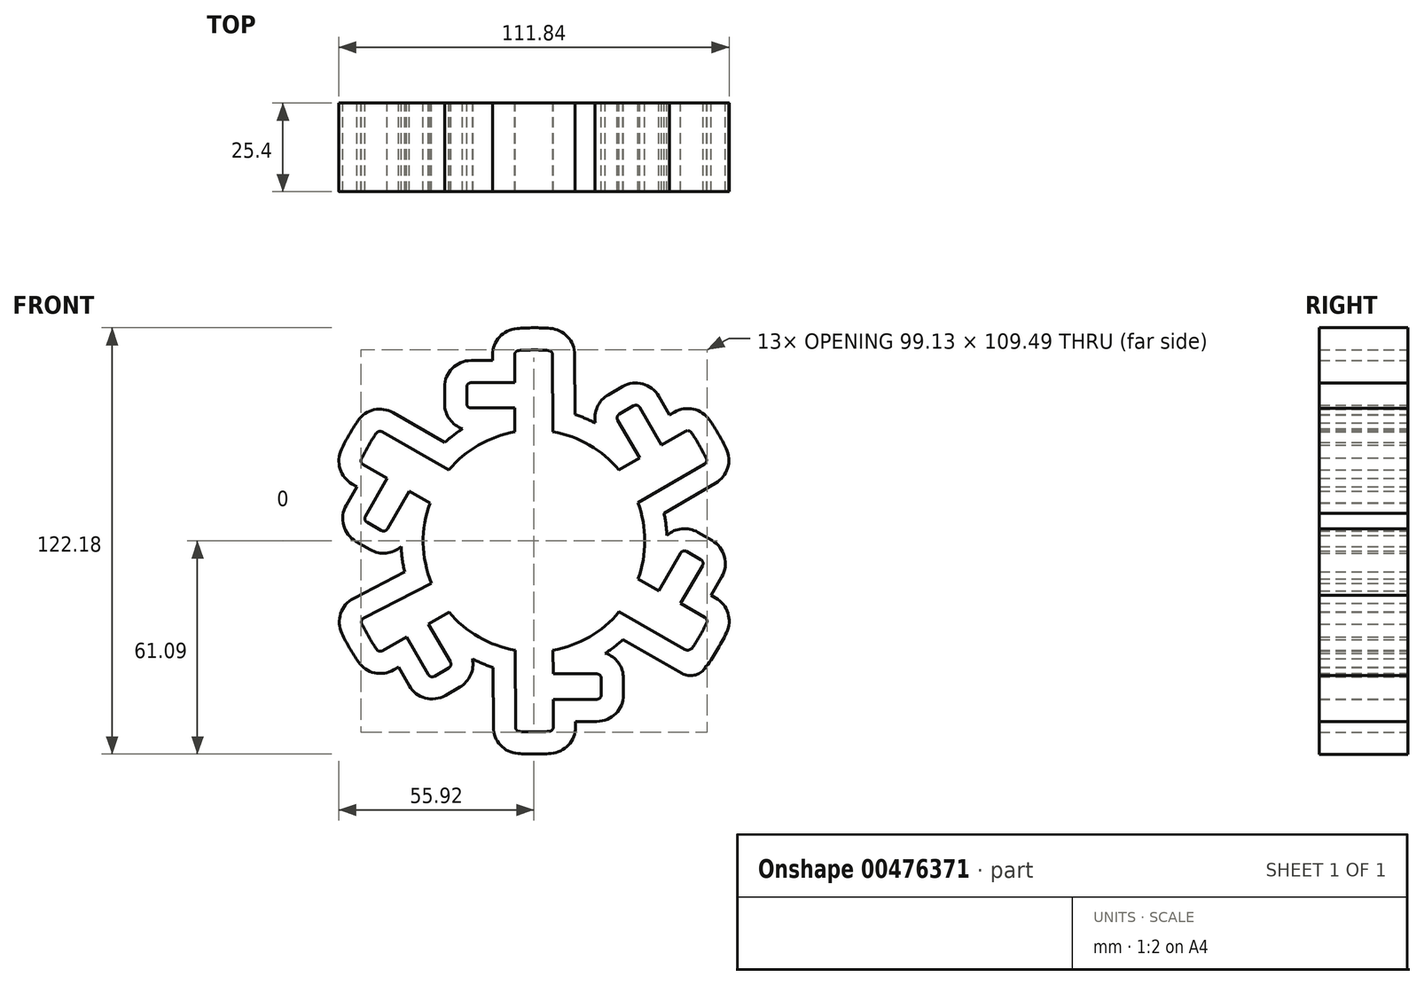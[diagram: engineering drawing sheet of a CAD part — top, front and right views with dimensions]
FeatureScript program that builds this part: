
annotation { "Feature Type Name" : "Feature", "Feature Type Description" : "" }
export const myFeature = defineFeature(function(context is Context, id is Id, definition is map)
    precondition{}
    {
        {
            var Q0;
            Q0=qCreatedBy(makeId("Front.planeOp"),FACE);
            var sketch = newSketch(context, id + "F0", { "sketchPlane" : qUnion([Q0])});
            skArc(sketch, "E0", {"start": v(5.31, 54.48) * mm, "mid": v(-0.12, 54.74) * mm, "end": v(-5.54, 54.46) * mm});
            skArc(sketch, "E1", {"start": v(-5.45, 31.28) * mm, "mid": v(-15.9, 27.48) * mm, "end": v(-24.4, 20.32) * mm});
            skLineSegment(sketch, "E2.left", {"start": v(-5.45, 31.28) * mm, "end": v(-5.48, 38.1) * mm});
            skLineSegment(sketch, "E2.right", {"start": v(5.4, 31.29) * mm, "end": v(5.31, 54.48) * mm});
            skLineSegment(sketch, "E3.bottom", {"start": v(-5.48, 38.1) * mm, "end": v(-19.28, 38.1) * mm});
            skLineSegment(sketch, "E3.top", {"start": v(-5.5, 45.36) * mm, "end": v(-19.28, 45.36) * mm});
            skLineSegment(sketch, "E3.left", {"start": v(5.38, 38.1) * mm, "end": v(5.38, 45.36) * mm});
            skLineSegment(sketch, "E3.right", {"start": v(-19.28, 38.1) * mm, "end": v(-19.28, 45.36) * mm});
            skLineSegment(sketch, "E4.trimOffspring", {"start": v(-5.5, 45.36) * mm, "end": v(-5.54, 54.46) * mm});
            skLineSegment(sketch, "E5.1.0", {"start": v(-30.3, 23.7) * mm, "end": v(-36.6, 27.34) * mm});
            skLineSegment(sketch, "E5.1.1", {"start": v(-24.4, 20.32) * mm, "end": v(-44.53, 31.84) * mm});
            skArc(sketch, "E5.1.2", {"start": v(-44.53, 31.84) * mm, "mid": v(-47.47, 27.27) * mm, "end": v(-49.94, 22.43) * mm});
            skLineSegment(sketch, "E5.1.3", {"start": v(-42.04, 17.9) * mm, "end": v(-49.94, 22.43) * mm});
            skLineSegment(sketch, "E5.1.4", {"start": v(-29.81, 10.92) * mm, "end": v(-35.74, 14.3) * mm});
            skLineSegment(sketch, "E5.1.5", {"start": v(-35.74, 14.3) * mm, "end": v(-42.64, 2.35) * mm});
            skLineSegment(sketch, "E5.1.6", {"start": v(-42.64, 2.35) * mm, "end": v(-48.92, 5.98) * mm});
            skLineSegment(sketch, "E5.1.7", {"start": v(-42.04, 17.9) * mm, "end": v(-48.92, 5.98) * mm});
            skArc(sketch, "E5.2.2", {"start": v(-49.84, -22.64) * mm, "mid": v(-47.35, -27.47) * mm, "end": v(-44.4, -32.03) * mm});
            skLineSegment(sketch, "E5.2.3", {"start": v(-36.53, -27.45) * mm, "end": v(-44.4, -32.03) * mm});
            skLineSegment(sketch, "E5.2.4", {"start": v(-24.36, -20.36) * mm, "end": v(-30.26, -23.8) * mm});
            skLineSegment(sketch, "E5.2.5", {"start": v(-30.26, -23.8) * mm, "end": v(-23.35, -35.75) * mm});
            skLineSegment(sketch, "E5.2.6", {"start": v(-23.35, -35.75) * mm, "end": v(-29.64, -39.38) * mm});
            skLineSegment(sketch, "E5.2.7", {"start": v(-36.53, -27.45) * mm, "end": v(-29.64, -39.38) * mm});
            skLineSegment(sketch, "E5.3.1", {"start": v(-5.4, -31.29) * mm, "end": v(-5.31, -54.48) * mm});
            skArc(sketch, "E5.3.2", {"start": v(-5.31, -54.48) * mm, "mid": v(0.12, -54.74) * mm, "end": v(5.54, -54.46) * mm});
            skLineSegment(sketch, "E5.3.3", {"start": v(5.5, -45.36) * mm, "end": v(5.54, -54.46) * mm});
            skLineSegment(sketch, "E5.3.4", {"start": v(5.45, -31.28) * mm, "end": v(5.48, -38.1) * mm});
            skLineSegment(sketch, "E5.3.5", {"start": v(5.48, -38.1) * mm, "end": v(19.28, -38.1) * mm});
            skLineSegment(sketch, "E5.3.6", {"start": v(19.28, -38.1) * mm, "end": v(19.28, -45.36) * mm});
            skLineSegment(sketch, "E5.3.7", {"start": v(5.5, -45.36) * mm, "end": v(19.28, -45.36) * mm});
            skLineSegment(sketch, "E5.4.0", {"start": v(30.3, -23.7) * mm, "end": v(36.6, -27.34) * mm});
            skLineSegment(sketch, "E5.4.1", {"start": v(24.4, -20.32) * mm, "end": v(44.53, -31.84) * mm});
            skArc(sketch, "E5.4.2", {"start": v(44.53, -31.84) * mm, "mid": v(47.47, -27.27) * mm, "end": v(49.94, -22.43) * mm});
            skLineSegment(sketch, "E5.4.3", {"start": v(42.04, -17.9) * mm, "end": v(49.94, -22.43) * mm});
            skLineSegment(sketch, "E5.4.4", {"start": v(29.81, -10.92) * mm, "end": v(35.74, -14.3) * mm});
            skLineSegment(sketch, "E5.4.5", {"start": v(35.74, -14.3) * mm, "end": v(42.64, -2.35) * mm});
            skLineSegment(sketch, "E5.4.6", {"start": v(42.64, -2.35) * mm, "end": v(48.92, -5.98) * mm});
            skLineSegment(sketch, "E5.4.7", {"start": v(42.04, -17.9) * mm, "end": v(48.92, -5.98) * mm});
            skLineSegment(sketch, "E6.3.5.0", {"start": v(29.8, 10.96) * mm, "end": v(49.84, 22.64) * mm});
            skArc(sketch, "E6.6.5.0", {"start": v(49.84, 22.64) * mm, "mid": v(47.35, 27.47) * mm, "end": v(44.4, 32.03) * mm});
            skLineSegment(sketch, "E6.10.5.0", {"start": v(36.53, 27.45) * mm, "end": v(44.4, 32.03) * mm});
            skLineSegment(sketch, "E6.13.5.0", {"start": v(24.36, 20.36) * mm, "end": v(30.26, 23.8) * mm});
            skLineSegment(sketch, "E6.16.5.0", {"start": v(30.26, 23.8) * mm, "end": v(23.35, 35.75) * mm});
            skLineSegment(sketch, "E6.19.5.0", {"start": v(23.35, 35.75) * mm, "end": v(29.64, 39.38) * mm});
            skLineSegment(sketch, "E6.22.5.0", {"start": v(36.53, 27.45) * mm, "end": v(29.64, 39.38) * mm});
            skLineSegment(sketch, "E7", {"start": v(-49.84, -22.64) * mm, "end": v(-29.37, -12.07) * mm});
            skArc(sketch, "E8.trimOffspring", {"start": v(24.36, 20.36) * mm, "mid": v(15.85, 27.5) * mm, "end": v(5.4, 31.29) * mm});
            skArc(sketch, "E9.trimOffspring", {"start": v(29.81, -10.92) * mm, "mid": v(31.75, 0.03) * mm, "end": v(29.8, 10.96) * mm});
            skArc(sketch, "E10.trimOffspring", {"start": v(5.45, -31.28) * mm, "mid": v(15.9, -27.48) * mm, "end": v(24.4, -20.32) * mm});
            skArc(sketch, "E11.trimOffspring", {"start": v(-24.36, -20.36) * mm, "mid": v(-15.85, -27.5) * mm, "end": v(-5.4, -31.29) * mm});
            skArc(sketch, "E12.trimOffspring", {"start": v(-29.81, 10.92) * mm, "mid": v(-31.74, -0.62) * mm, "end": v(-29.37, -12.07) * mm});
            skSolve(sketch);
        }
        {
            var Q0;
            {var subQ0=sQuery(id+"F0.wireOp",EDGE,"E1");var subQ5=makeQuery(id+"F0.imprint","INTERSECT",VERTEX,{"derivedFrom":[subQ0,sQuery(id+"F0.wireOp",EDGE,"E5.4.1")]});Q0=makeQuery(id+"F0.imprint","IMPRINT",FACE,{"disambiguationData":[TD([[makeQuery(id+"F0.imprint","IMPRINT",EDGE,{"disambiguationData":[TD([[subQ5,-1.0]])],"derivedFrom":subQ0}),1.0]])]});}
            var Q1;
            {var subQ0=sQuery(id+"F0.wireOp",EDGE,"E5.1.2");Q1=makeQuery(id+"F0.imprint","IMPRINT",FACE,{"disambiguationData":[TD([[makeQuery(id+"F0.imprint","IMPRINT",EDGE,{"derivedFrom":subQ0}),1.0]])]});}
            var Q2;
            {var subQ5=sQuery(id+"F0.wireOp",EDGE,"E0");Q2=makeQuery(id+"F0.imprint","IMPRINT",FACE,{"disambiguationData":[TD([[makeQuery(id+"F0.imprint","IMPRINT",EDGE,{"derivedFrom":subQ5}),1.0]])]});}
            var Q3;
            {var subQ0=sQuery(id+"F0.wireOp",EDGE,"E5.4.2");Q3=makeQuery(id+"F0.imprint","IMPRINT",FACE,{"disambiguationData":[TD([[makeQuery(id+"F0.imprint","IMPRINT",EDGE,{"derivedFrom":subQ0}),1.0]])]});}
            var Q4;
            {var subQ0=sQuery(id+"F0.wireOp",EDGE,"E5.3.2");Q4=makeQuery(id+"F0.imprint","IMPRINT",FACE,{"disambiguationData":[TD([[makeQuery(id+"F0.imprint","IMPRINT",EDGE,{"derivedFrom":subQ0}),1.0]])]});}
            var Q5;
            {var subQ0=sQuery(id+"F0.wireOp",EDGE,"E5.2.2");Q5=makeQuery(id+"F0.imprint","IMPRINT",FACE,{"disambiguationData":[TD([[makeQuery(id+"F0.imprint","IMPRINT",EDGE,{"derivedFrom":subQ0}),1.0]])]});}
            var Q6;
            {var subQ0=sQuery(id+"F0.wireOp",EDGE,"E6.6.5.0");Q6=makeQuery(id+"F0.imprint","IMPRINT",FACE,{"disambiguationData":[TD([[makeQuery(id+"F0.imprint","IMPRINT",EDGE,{"derivedFrom":subQ0}),1.0]])]});}
            extrude(context, id + "F1", {"entities" : qUnion([Q0, Q1, Q2, Q3, Q4, Q5, Q6]), "depth" : 25.4 * mm});
        }
        {
            var Q0;
            Q0=makeQuery(id+"F1.opExtrude","SWEPT_EDGE",EDGE,{"disambiguationData":[OSD([sQuery(id+"F0.wireOp",EDGE,"E0"),sQuery(id+"F0.wireOp",EDGE,"E2.right")])]});
            var Q1;
            Q1=makeQuery(id+"F1.opExtrude","SWEPT_EDGE",EDGE,{"disambiguationData":[OSD([sQuery(id+"F0.wireOp",EDGE,"E0"),sQuery(id+"F0.wireOp",EDGE,"E4.trimOffspring")])]});
            fillet(context, id + "F2", {"entities" : qUnion([Q0, Q1]), "radius" : 1.27 * mm, "tangentPropagation" : true, "allowEdgeOverflow" : false});
        }
        {
            var Q0;
            Q0=makeQuery(id+"F1.opExtrude","SWEPT_EDGE",EDGE,{"disambiguationData":[OSD([sQuery(id+"F0.wireOp",EDGE,"E3.top"),sQuery(id+"F0.wireOp",EDGE,"E3.right")])]});
            var Q1;
            Q1=makeQuery(id+"F1.opExtrude","SWEPT_EDGE",EDGE,{"disambiguationData":[OSD([sQuery(id+"F0.wireOp",EDGE,"E3.bottom"),sQuery(id+"F0.wireOp",EDGE,"E3.right")])]});
            fillet(context, id + "F3", {"entities" : qUnion([Q0, Q1]), "radius" : 1.27 * mm, "tangentPropagation" : true, "allowEdgeOverflow" : false});
        }
        {
            var Q0;
            Q0=makeQuery(id+"F1.opExtrude","SWEPT_EDGE",EDGE,{"disambiguationData":[OSD([sQuery(id+"F0.wireOp",EDGE,"E6.19.5.0"),sQuery(id+"F0.wireOp",EDGE,"E6.22.5.0")])]});
            var Q1;
            Q1=makeQuery(id+"F1.opExtrude","SWEPT_EDGE",EDGE,{"disambiguationData":[OSD([sQuery(id+"F0.wireOp",EDGE,"E6.16.5.0"),sQuery(id+"F0.wireOp",EDGE,"E6.19.5.0")])]});
            var Q2;
            Q2=makeQuery(id+"F1.opExtrude","SWEPT_EDGE",EDGE,{"disambiguationData":[OSD([sQuery(id+"F0.wireOp",EDGE,"E6.6.5.0"),sQuery(id+"F0.wireOp",EDGE,"E6.10.5.0")])]});
            var Q3;
            Q3=makeQuery(id+"F1.opExtrude","SWEPT_EDGE",EDGE,{"disambiguationData":[OSD([sQuery(id+"F0.wireOp",EDGE,"E6.3.5.0"),sQuery(id+"F0.wireOp",EDGE,"E6.6.5.0")])]});
            var Q4;
            Q4=makeQuery(id+"F1.opExtrude","SWEPT_EDGE",EDGE,{"disambiguationData":[OSD([sQuery(id+"F0.wireOp",EDGE,"E5.4.6"),sQuery(id+"F0.wireOp",EDGE,"E5.4.7")])]});
            var Q5;
            Q5=makeQuery(id+"F1.opExtrude","SWEPT_EDGE",EDGE,{"disambiguationData":[OSD([sQuery(id+"F0.wireOp",EDGE,"E5.4.2"),sQuery(id+"F0.wireOp",EDGE,"E5.4.3")])]});
            var Q6;
            Q6=makeQuery(id+"F1.opExtrude","SWEPT_EDGE",EDGE,{"disambiguationData":[OSD([sQuery(id+"F0.wireOp",EDGE,"E5.4.5"),sQuery(id+"F0.wireOp",EDGE,"E5.4.6")])]});
            var Q7;
            Q7=makeQuery(id+"F1.opExtrude","SWEPT_EDGE",EDGE,{"disambiguationData":[OSD([sQuery(id+"F0.wireOp",EDGE,"E5.3.6"),sQuery(id+"F0.wireOp",EDGE,"E5.3.7")])]});
            var Q8;
            Q8=makeQuery(id+"F1.opExtrude","SWEPT_EDGE",EDGE,{"disambiguationData":[OSD([sQuery(id+"F0.wireOp",EDGE,"E5.3.5"),sQuery(id+"F0.wireOp",EDGE,"E5.3.6")])]});
            var Q9;
            Q9=makeQuery(id+"F1.opExtrude","SWEPT_EDGE",EDGE,{"disambiguationData":[OSD([sQuery(id+"F0.wireOp",EDGE,"E5.3.2"),sQuery(id+"F0.wireOp",EDGE,"E5.3.3")])]});
            var Q10;
            Q10=makeQuery(id+"F1.opExtrude","SWEPT_EDGE",EDGE,{"disambiguationData":[OSD([sQuery(id+"F0.wireOp",EDGE,"E5.3.1"),sQuery(id+"F0.wireOp",EDGE,"E5.3.2")])]});
            var Q11;
            Q11=makeQuery(id+"F1.opExtrude","SWEPT_EDGE",EDGE,{"disambiguationData":[OSD([sQuery(id+"F0.wireOp",EDGE,"E5.2.6"),sQuery(id+"F0.wireOp",EDGE,"E5.2.7")])]});
            var Q12;
            Q12=makeQuery(id+"F1.opExtrude","SWEPT_EDGE",EDGE,{"disambiguationData":[OSD([sQuery(id+"F0.wireOp",EDGE,"E5.2.5"),sQuery(id+"F0.wireOp",EDGE,"E5.2.6")])]});
            var Q13;
            Q13=makeQuery(id+"F1.opExtrude","SWEPT_EDGE",EDGE,{"disambiguationData":[OSD([sQuery(id+"F0.wireOp",EDGE,"E5.2.2"),sQuery(id+"F0.wireOp",EDGE,"E5.2.3")])]});
            var Q14;
            Q14=makeQuery(id+"F1.opExtrude","SWEPT_EDGE",EDGE,{"disambiguationData":[OSD([sQuery(id+"F0.wireOp",EDGE,"E5.2.1"),sQuery(id+"F0.wireOp",EDGE,"E5.2.2")])]});
            var Q15;
            Q15=makeQuery(id+"F1.opExtrude","SWEPT_EDGE",EDGE,{"disambiguationData":[OSD([sQuery(id+"F0.wireOp",EDGE,"E5.1.6"),sQuery(id+"F0.wireOp",EDGE,"E5.1.7")])]});
            var Q16;
            Q16=makeQuery(id+"F1.opExtrude","SWEPT_EDGE",EDGE,{"disambiguationData":[OSD([sQuery(id+"F0.wireOp",EDGE,"E5.1.5"),sQuery(id+"F0.wireOp",EDGE,"E5.1.6")])]});
            var Q17;
            Q17=makeQuery(id+"F1.opExtrude","SWEPT_EDGE",EDGE,{"disambiguationData":[OSD([sQuery(id+"F0.wireOp",EDGE,"E5.1.2"),sQuery(id+"F0.wireOp",EDGE,"E5.1.3")])]});
            var Q18;
            Q18=makeQuery(id+"F1.opExtrude","SWEPT_EDGE",EDGE,{"disambiguationData":[OSD([sQuery(id+"F0.wireOp",EDGE,"E5.1.1"),sQuery(id+"F0.wireOp",EDGE,"E5.1.2")])]});
            fillet(context, id + "F4", {"entities" : qUnion([Q0, Q1, Q2, Q3, Q4, Q5, Q6, Q7, Q8, Q9, Q10, Q11, Q12, Q13, Q14, Q15, Q16, Q17, Q18]), "radius" : 1.27 * mm, "tangentPropagation" : true, "allowEdgeOverflow" : false});
        }
        {
            var Q0;
            Q0=makeQuery(id+"F1.opExtrude","CAP_FACE",FACE,{"disambiguationData":[OSD([sQuery(id+"F0.wireOp",EDGE,"E0"),sQuery(id+"F0.wireOp",EDGE,"E1"),sQuery(id+"F0.wireOp",EDGE,"E2.left"),sQuery(id+"F0.wireOp",EDGE,"E2.right"),sQuery(id+"F0.wireOp",EDGE,"E3.bottom"),sQuery(id+"F0.wireOp",EDGE,"E3.top"),sQuery(id+"F0.wireOp",EDGE,"E3.right"),sQuery(id+"F0.wireOp",EDGE,"E4.trimOffspring"),sQuery(id+"F0.wireOp",EDGE,"E5.1.1"),sQuery(id+"F0.wireOp",EDGE,"E5.1.2"),sQuery(id+"F0.wireOp",EDGE,"E5.1.3"),sQuery(id+"F0.wireOp",EDGE,"E5.1.4"),sQuery(id+"F0.wireOp",EDGE,"E5.1.5"),sQuery(id+"F0.wireOp",EDGE,"E5.1.6"),sQuery(id+"F0.wireOp",EDGE,"E5.1.7"),sQuery(id+"F0.wireOp",EDGE,"E5.2.2"),sQuery(id+"F0.wireOp",EDGE,"E5.2.3"),sQuery(id+"F0.wireOp",EDGE,"E5.2.4"),sQuery(id+"F0.wireOp",EDGE,"E5.2.5"),sQuery(id+"F0.wireOp",EDGE,"E5.2.6"),sQuery(id+"F0.wireOp",EDGE,"E5.2.7"),sQuery(id+"F0.wireOp",EDGE,"E5.3.1"),sQuery(id+"F0.wireOp",EDGE,"E5.3.2"),sQuery(id+"F0.wireOp",EDGE,"E5.3.3"),sQuery(id+"F0.wireOp",EDGE,"E5.3.4"),sQuery(id+"F0.wireOp",EDGE,"E5.3.5"),sQuery(id+"F0.wireOp",EDGE,"E5.3.6"),sQuery(id+"F0.wireOp",EDGE,"E5.3.7"),sQuery(id+"F0.wireOp",EDGE,"E5.4.1"),sQuery(id+"F0.wireOp",EDGE,"E5.4.2"),sQuery(id+"F0.wireOp",EDGE,"E5.4.3"),sQuery(id+"F0.wireOp",EDGE,"E5.4.4"),sQuery(id+"F0.wireOp",EDGE,"E5.4.5"),sQuery(id+"F0.wireOp",EDGE,"E5.4.6"),sQuery(id+"F0.wireOp",EDGE,"E5.4.7"),sQuery(id+"F0.wireOp",EDGE,"E6.3.5.0"),sQuery(id+"F0.wireOp",EDGE,"E6.6.5.0"),sQuery(id+"F0.wireOp",EDGE,"E6.10.5.0"),sQuery(id+"F0.wireOp",EDGE,"E6.13.5.0"),sQuery(id+"F0.wireOp",EDGE,"E6.16.5.0"),sQuery(id+"F0.wireOp",EDGE,"E6.19.5.0"),sQuery(id+"F0.wireOp",EDGE,"E6.22.5.0"),sQuery(id+"F0.wireOp",EDGE,"E7"),sQuery(id+"F0.wireOp",EDGE,"E8.trimOffspring"),sQuery(id+"F0.wireOp",EDGE,"E9.trimOffspring"),sQuery(id+"F0.wireOp",EDGE,"E10.trimOffspring"),sQuery(id+"F0.wireOp",EDGE,"E11.trimOffspring"),sQuery(id+"F0.wireOp",EDGE,"E12.trimOffspring")])],"isStart":false});
            var sketch = newSketch(context, id + "F5", { "sketchPlane" : qUnion([Q0])});
            skLineSegment(sketch, "E13.0.0", {"start": v(-24.4, 20.32) * mm, "end": v(-43.52, 31.27) * mm});
            skArc(sketch, "E13.0.1", {"start": v(-43.52, 31.27) * mm, "mid": v(-44.44, 31.4) * mm, "end": v(-45.2, 30.88) * mm});
            skArc(sketch, "E13.0.2", {"start": v(-45.2, 30.88) * mm, "mid": v(-47.47, 27.27) * mm, "end": v(-49.44, 23.5) * mm});
            skArc(sketch, "E13.0.3", {"start": v(-49.44, 23.5) * mm, "mid": v(-49.5, 22.57) * mm, "end": v(-48.93, 21.85) * mm});
            skLineSegment(sketch, "E13.0.4", {"start": v(-48.93, 21.85) * mm, "end": v(-42.04, 17.9) * mm});
            skLineSegment(sketch, "E13.0.5", {"start": v(-42.04, 17.9) * mm, "end": v(-48.29, 7.08) * mm});
            skArc(sketch, "E13.0.6", {"start": v(-48.29, 7.08) * mm, "mid": v(-48.42, 6.12) * mm, "end": v(-47.82, 5.34) * mm});
            skLineSegment(sketch, "E13.0.7", {"start": v(-47.82, 5.34) * mm, "end": v(-43.74, 2.98) * mm});
            skArc(sketch, "E13.0.8", {"start": v(-43.74, 2.98) * mm, "mid": v(-42.77, 2.86) * mm, "end": v(-42, 3.45) * mm});
            skLineSegment(sketch, "E13.0.9", {"start": v(-42, 3.45) * mm, "end": v(-35.74, 14.3) * mm});
            skLineSegment(sketch, "E13.0.10", {"start": v(-35.74, 14.3) * mm, "end": v(-29.81, 10.92) * mm});
            skArc(sketch, "E13.0.11", {"start": v(-29.81, 10.92) * mm, "mid": v(-31.74, -0.62) * mm, "end": v(-29.37, -12.07) * mm});
            skLineSegment(sketch, "E13.0.12", {"start": v(-29.37, -12.07) * mm, "end": v(-48.76, -22.08) * mm});
            skArc(sketch, "E13.0.13", {"start": v(-48.76, -22.08) * mm, "mid": v(-49.38, -22.8) * mm, "end": v(-49.32, -23.76) * mm});
            skArc(sketch, "E13.0.14", {"start": v(-49.32, -23.76) * mm, "mid": v(-47.34, -27.5) * mm, "end": v(-45.07, -31.07) * mm});
            skArc(sketch, "E13.0.15", {"start": v(-45.07, -31.07) * mm, "mid": v(-44.3, -31.59) * mm, "end": v(-43.39, -31.45) * mm});
            skLineSegment(sketch, "E13.0.16", {"start": v(-43.39, -31.45) * mm, "end": v(-36.53, -27.45) * mm});
            skLineSegment(sketch, "E13.0.17", {"start": v(-36.53, -27.45) * mm, "end": v(-30.28, -38.28) * mm});
            skArc(sketch, "E13.0.18", {"start": v(-30.28, -38.28) * mm, "mid": v(-29.5, -38.87) * mm, "end": v(-28.54, -38.75) * mm});
            skLineSegment(sketch, "E13.0.19", {"start": v(-28.54, -38.75) * mm, "end": v(-24.45, -36.39) * mm});
            skArc(sketch, "E13.0.20", {"start": v(-24.45, -36.39) * mm, "mid": v(-23.86, -35.61) * mm, "end": v(-23.99, -34.65) * mm});
            skLineSegment(sketch, "E13.0.21", {"start": v(-23.99, -34.65) * mm, "end": v(-30.26, -23.8) * mm});
            skLineSegment(sketch, "E13.0.22", {"start": v(-30.26, -23.8) * mm, "end": v(-24.36, -20.36) * mm});
            skArc(sketch, "E13.0.23", {"start": v(-24.36, -20.36) * mm, "mid": v(-15.85, -27.5) * mm, "end": v(-5.4, -31.29) * mm});
            skLineSegment(sketch, "E13.0.24", {"start": v(-5.4, -31.29) * mm, "end": v(-5.32, -53.32) * mm});
            skArc(sketch, "E13.0.25", {"start": v(-5.32, -53.32) * mm, "mid": v(-4.98, -54.19) * mm, "end": v(-4.14, -54.59) * mm});
            skArc(sketch, "E13.0.26", {"start": v(-4.14, -54.59) * mm, "mid": v(0.12, -54.74) * mm, "end": v(4.37, -54.57) * mm});
            skArc(sketch, "E13.0.27", {"start": v(4.37, -54.57) * mm, "mid": v(5.2, -54.16) * mm, "end": v(5.54, -53.3) * mm});
            skLineSegment(sketch, "E13.0.28", {"start": v(5.54, -53.3) * mm, "end": v(5.5, -45.36) * mm});
            skLineSegment(sketch, "E13.0.29", {"start": v(5.5, -45.36) * mm, "end": v(18.01, -45.36) * mm});
            skArc(sketch, "E13.0.30", {"start": v(18.01, -45.36) * mm, "mid": v(18.91, -44.99) * mm, "end": v(19.28, -44.1) * mm});
            skLineSegment(sketch, "E13.0.31", {"start": v(19.28, -44.1) * mm, "end": v(19.28, -39.37) * mm});
            skArc(sketch, "E13.0.32", {"start": v(19.28, -39.37) * mm, "mid": v(18.91, -38.47) * mm, "end": v(18.01, -38.1) * mm});
            skLineSegment(sketch, "E13.0.33", {"start": v(18.01, -38.1) * mm, "end": v(5.48, -38.1) * mm});
            skLineSegment(sketch, "E13.0.34", {"start": v(5.48, -38.1) * mm, "end": v(5.45, -31.28) * mm});
            skArc(sketch, "E13.0.35", {"start": v(5.45, -31.28) * mm, "mid": v(15.9, -27.48) * mm, "end": v(24.4, -20.32) * mm});
            skLineSegment(sketch, "E13.0.36", {"start": v(24.4, -20.32) * mm, "end": v(44.53, -31.84) * mm});
            skArc(sketch, "E13.0.37", {"start": v(44.53, -31.84) * mm, "mid": v(47.17, -27.78) * mm, "end": v(49.44, -23.5) * mm});
            skArc(sketch, "E13.0.38", {"start": v(49.44, -23.5) * mm, "mid": v(49.5, -22.57) * mm, "end": v(48.93, -21.85) * mm});
            skLineSegment(sketch, "E13.0.39", {"start": v(48.93, -21.85) * mm, "end": v(42.04, -17.9) * mm});
            skLineSegment(sketch, "E13.0.40", {"start": v(42.04, -17.9) * mm, "end": v(48.29, -7.08) * mm});
            skArc(sketch, "E13.0.41", {"start": v(48.29, -7.08) * mm, "mid": v(48.42, -6.12) * mm, "end": v(47.82, -5.34) * mm});
            skLineSegment(sketch, "E13.0.42", {"start": v(47.82, -5.34) * mm, "end": v(43.74, -2.98) * mm});
            skArc(sketch, "E13.0.43", {"start": v(43.74, -2.98) * mm, "mid": v(42.77, -2.86) * mm, "end": v(42, -3.45) * mm});
            skLineSegment(sketch, "E13.0.44", {"start": v(42, -3.45) * mm, "end": v(35.74, -14.3) * mm});
            skLineSegment(sketch, "E13.0.45", {"start": v(35.74, -14.3) * mm, "end": v(29.81, -10.92) * mm});
            skArc(sketch, "E13.0.46", {"start": v(29.81, -10.92) * mm, "mid": v(31.75, 0.03) * mm, "end": v(29.8, 10.96) * mm});
            skLineSegment(sketch, "E13.0.47", {"start": v(29.8, 10.96) * mm, "end": v(48.84, 22.06) * mm});
            skArc(sketch, "E13.0.48", {"start": v(48.84, 22.06) * mm, "mid": v(49.41, 22.78) * mm, "end": v(49.34, 23.7) * mm});
            skArc(sketch, "E13.0.49", {"start": v(49.34, 23.7) * mm, "mid": v(47.35, 27.47) * mm, "end": v(45.07, 31.07) * mm});
            skArc(sketch, "E13.0.50", {"start": v(45.07, 31.07) * mm, "mid": v(44.3, 31.59) * mm, "end": v(43.39, 31.45) * mm});
            skLineSegment(sketch, "E13.0.51", {"start": v(43.39, 31.45) * mm, "end": v(36.53, 27.45) * mm});
            skLineSegment(sketch, "E13.0.52", {"start": v(36.53, 27.45) * mm, "end": v(30.28, 38.28) * mm});
            skArc(sketch, "E13.0.53", {"start": v(30.28, 38.28) * mm, "mid": v(29.5, 38.87) * mm, "end": v(28.54, 38.75) * mm});
            skLineSegment(sketch, "E13.0.54", {"start": v(28.54, 38.75) * mm, "end": v(24.45, 36.39) * mm});
            skArc(sketch, "E13.0.55", {"start": v(24.45, 36.39) * mm, "mid": v(23.86, 35.61) * mm, "end": v(23.99, 34.65) * mm});
            skLineSegment(sketch, "E13.0.56", {"start": v(23.99, 34.65) * mm, "end": v(30.26, 23.8) * mm});
            skLineSegment(sketch, "E13.0.57", {"start": v(30.26, 23.8) * mm, "end": v(24.36, 20.36) * mm});
            skArc(sketch, "E13.0.58", {"start": v(24.36, 20.36) * mm, "mid": v(15.85, 27.5) * mm, "end": v(5.4, 31.29) * mm});
            skLineSegment(sketch, "E13.0.59", {"start": v(5.4, 31.29) * mm, "end": v(5.32, 53.32) * mm});
            skArc(sketch, "E13.0.60", {"start": v(5.32, 53.32) * mm, "mid": v(4.98, 54.19) * mm, "end": v(4.14, 54.59) * mm});
            skArc(sketch, "E13.0.61", {"start": v(4.14, 54.59) * mm, "mid": v(-0.12, 54.74) * mm, "end": v(-4.37, 54.57) * mm});
            skArc(sketch, "E13.0.62", {"start": v(-4.37, 54.57) * mm, "mid": v(-5.2, 54.16) * mm, "end": v(-5.54, 53.3) * mm});
            skLineSegment(sketch, "E13.0.63", {"start": v(-5.54, 53.3) * mm, "end": v(-5.5, 45.36) * mm});
            skLineSegment(sketch, "E13.0.64", {"start": v(-5.5, 45.36) * mm, "end": v(-18.01, 45.36) * mm});
            skArc(sketch, "E13.0.65", {"start": v(-18.01, 45.36) * mm, "mid": v(-18.91, 44.99) * mm, "end": v(-19.28, 44.1) * mm});
            skLineSegment(sketch, "E13.0.66", {"start": v(-19.28, 44.1) * mm, "end": v(-19.28, 39.37) * mm});
            skArc(sketch, "E13.0.67", {"start": v(-19.28, 39.37) * mm, "mid": v(-18.91, 38.47) * mm, "end": v(-18.01, 38.1) * mm});
            skLineSegment(sketch, "E13.0.68", {"start": v(-18.01, 38.1) * mm, "end": v(-5.48, 38.1) * mm});
            skLineSegment(sketch, "E13.0.69", {"start": v(-5.48, 38.1) * mm, "end": v(-5.45, 31.28) * mm});
            skArc(sketch, "E13.0.70", {"start": v(-5.45, 31.28) * mm, "mid": v(-15.9, 27.48) * mm, "end": v(-24.4, 20.32) * mm});
            skLineSegment(sketch, "E14.0", {"start": v(-25.52, 28.29) * mm, "end": v(-40.37, 36.78) * mm});
            skArc(sketch, "E14.1", {"start": v(-20.45, 32.15) * mm, "mid": v(-23.07, 30.32) * mm, "end": v(-25.52, 28.29) * mm});
            skArc(sketch, "E14.2", {"start": v(-25.63, 39.37) * mm, "mid": v(-24.2, 34.92) * mm, "end": v(-20.45, 32.15) * mm});
            skLineSegment(sketch, "E14.3", {"start": v(-25.63, 44.1) * mm, "end": v(-25.63, 39.37) * mm});
            skArc(sketch, "E14.4", {"start": v(-18.01, 51.71) * mm, "mid": v(-23.4, 49.48) * mm, "end": v(-25.63, 44.1) * mm});
            skLineSegment(sketch, "E14.5", {"start": v(-11.88, 51.71) * mm, "end": v(-18.01, 51.71) * mm});
            skLineSegment(sketch, "E14.6", {"start": v(-11.9, 53.27) * mm, "end": v(-11.88, 51.71) * mm});
            skArc(sketch, "E14.7", {"start": v(-4.88, 60.9) * mm, "mid": v(-9.88, 58.46) * mm, "end": v(-11.9, 53.27) * mm});
            skArc(sketch, "E14.8", {"start": v(4.62, 60.92) * mm, "mid": v(-0.13, 61.1) * mm, "end": v(-4.88, 60.9) * mm});
            skArc(sketch, "E14.9", {"start": v(11.67, 53.35) * mm, "mid": v(9.62, 58.51) * mm, "end": v(4.62, 60.92) * mm});
            skLineSegment(sketch, "E14.10", {"start": v(11.73, 36.25) * mm, "end": v(11.67, 53.35) * mm});
            skArc(sketch, "E14.11", {"start": v(17.62, 33.78) * mm, "mid": v(14.73, 35.14) * mm, "end": v(11.73, 36.25) * mm});
            skArc(sketch, "E14.12", {"start": v(21.28, 41.88) * mm, "mid": v(18.14, 38.42) * mm, "end": v(17.62, 33.78) * mm});
            skArc(sketch, "E14.13", {"start": v(-4.62, -60.92) * mm, "mid": v(0.13, -61.1) * mm, "end": v(4.88, -60.9) * mm});
            skArc(sketch, "E14.14", {"start": v(-11.67, -53.35) * mm, "mid": v(-9.62, -58.51) * mm, "end": v(-4.62, -60.92) * mm});
            skLineSegment(sketch, "E14.15", {"start": v(-11.73, -36.25) * mm, "end": v(-11.67, -53.35) * mm});
            skArc(sketch, "E14.16", {"start": v(-17.62, -33.78) * mm, "mid": v(-14.73, -35.14) * mm, "end": v(-11.73, -36.25) * mm});
            skArc(sketch, "E14.17", {"start": v(-21.28, -41.88) * mm, "mid": v(-18.14, -38.42) * mm, "end": v(-17.62, -33.78) * mm});
            skLineSegment(sketch, "E14.18", {"start": v(-25.37, -44.24) * mm, "end": v(-21.28, -41.88) * mm});
            skArc(sketch, "E14.19", {"start": v(-35.78, -41.46) * mm, "mid": v(-31.15, -45) * mm, "end": v(-25.37, -44.24) * mm});
            skLineSegment(sketch, "E14.20", {"start": v(-38.84, -36.15) * mm, "end": v(-35.78, -41.46) * mm});
            skLineSegment(sketch, "E14.21", {"start": v(-40.2, -36.93) * mm, "end": v(-38.84, -36.15) * mm});
            skArc(sketch, "E14.22", {"start": v(-50.3, -34.67) * mm, "mid": v(-45.69, -37.79) * mm, "end": v(-40.2, -36.93) * mm});
            skArc(sketch, "E14.23", {"start": v(-55.04, -26.52) * mm, "mid": v(-52.83, -30.69) * mm, "end": v(-50.3, -34.67) * mm});
            skArc(sketch, "E14.24", {"start": v(-51.67, -16.44) * mm, "mid": v(-55.4, -20.8) * mm, "end": v(-55.04, -26.52) * mm});
            skLineSegment(sketch, "E14.25", {"start": v(-52.08, 16.34) * mm, "end": v(-50.72, 15.56) * mm});
            skArc(sketch, "E14.26", {"start": v(-55.18, 26.22) * mm, "mid": v(-55.57, 20.67) * mm, "end": v(-52.08, 16.34) * mm});
            skArc(sketch, "E14.27", {"start": v(-50.45, 34.46) * mm, "mid": v(-52.97, 30.44) * mm, "end": v(-55.18, 26.22) * mm});
            skArc(sketch, "E14.28", {"start": v(-40.37, 36.78) * mm, "mid": v(-45.86, 37.6) * mm, "end": v(-50.45, 34.46) * mm});
            skLineSegment(sketch, "E14.29", {"start": v(-50.72, 15.56) * mm, "end": v(-53.79, 10.25) * mm});
            skArc(sketch, "E14.30", {"start": v(-53.79, 10.25) * mm, "mid": v(-54.55, 4.47) * mm, "end": v(-51, -0.15) * mm});
            skLineSegment(sketch, "E14.31", {"start": v(-51, -0.15) * mm, "end": v(-46.91, -2.51) * mm});
            skArc(sketch, "E14.32", {"start": v(-46.91, -2.51) * mm, "mid": v(-42.35, -3.5) * mm, "end": v(-38.07, -1.63) * mm});
            skArc(sketch, "E14.33", {"start": v(-38.07, -1.63) * mm, "mid": v(-37.73, -5.29) * mm, "end": v(-37.05, -8.9) * mm});
            skLineSegment(sketch, "E14.34", {"start": v(-37.05, -8.9) * mm, "end": v(-51.67, -16.44) * mm});
            skArc(sketch, "E14.35", {"start": v(4.88, -60.9) * mm, "mid": v(9.88, -58.46) * mm, "end": v(11.9, -53.27) * mm});
            skLineSegment(sketch, "E14.36", {"start": v(11.9, -53.27) * mm, "end": v(11.88, -51.71) * mm});
            skLineSegment(sketch, "E14.37", {"start": v(11.88, -51.71) * mm, "end": v(18.01, -51.71) * mm});
            skArc(sketch, "E14.38", {"start": v(18.01, -51.71) * mm, "mid": v(23.4, -49.48) * mm, "end": v(25.63, -44.1) * mm});
            skLineSegment(sketch, "E14.39", {"start": v(25.63, -44.1) * mm, "end": v(25.63, -39.37) * mm});
            skArc(sketch, "E14.40", {"start": v(25.63, -39.37) * mm, "mid": v(24.2, -34.92) * mm, "end": v(20.45, -32.15) * mm});
            skArc(sketch, "E14.41", {"start": v(20.45, -32.15) * mm, "mid": v(23.07, -30.32) * mm, "end": v(25.52, -28.29) * mm});
            skLineSegment(sketch, "E14.42", {"start": v(25.52, -28.29) * mm, "end": v(46.12, -40.07) * mm});
            skArc(sketch, "E14.43", {"start": v(46.12, -40.07) * mm, "mid": v(51.12, -33.45) * mm, "end": v(55.18, -26.22) * mm});
            skArc(sketch, "E14.44", {"start": v(55.18, -26.22) * mm, "mid": v(55.57, -20.67) * mm, "end": v(52.08, -16.34) * mm});
            skLineSegment(sketch, "E14.45", {"start": v(52.08, -16.34) * mm, "end": v(50.72, -15.56) * mm});
            skLineSegment(sketch, "E14.46", {"start": v(50.72, -15.56) * mm, "end": v(53.79, -10.25) * mm});
            skArc(sketch, "E14.47", {"start": v(53.79, -10.25) * mm, "mid": v(54.55, -4.47) * mm, "end": v(51, 0.15) * mm});
            skLineSegment(sketch, "E14.48", {"start": v(51, 0.15) * mm, "end": v(46.91, 2.51) * mm});
            skArc(sketch, "E14.49", {"start": v(46.91, 2.51) * mm, "mid": v(42.35, 3.5) * mm, "end": v(38.07, 1.63) * mm});
            skArc(sketch, "E14.50", {"start": v(38.07, 1.63) * mm, "mid": v(37.8, 4.81) * mm, "end": v(37.26, 7.96) * mm});
            skLineSegment(sketch, "E14.51", {"start": v(37.26, 7.96) * mm, "end": v(52.04, 16.57) * mm});
            skArc(sketch, "E14.52", {"start": v(52.04, 16.57) * mm, "mid": v(55.48, 20.92) * mm, "end": v(55.07, 26.46) * mm});
            skArc(sketch, "E14.53", {"start": v(55.07, 26.46) * mm, "mid": v(52.84, 30.66) * mm, "end": v(50.3, 34.67) * mm});
            skArc(sketch, "E14.54", {"start": v(50.3, 34.67) * mm, "mid": v(45.69, 37.79) * mm, "end": v(40.2, 36.93) * mm});
            skLineSegment(sketch, "E14.55", {"start": v(40.2, 36.93) * mm, "end": v(38.84, 36.15) * mm});
            skLineSegment(sketch, "E14.56", {"start": v(38.84, 36.15) * mm, "end": v(35.78, 41.46) * mm});
            skArc(sketch, "E14.57", {"start": v(35.78, 41.46) * mm, "mid": v(31.15, 45) * mm, "end": v(25.37, 44.24) * mm});
            skLineSegment(sketch, "E14.58", {"start": v(25.37, 44.24) * mm, "end": v(21.28, 41.88) * mm});
            skSolve(sketch);
        }
        {
            var Q0;
            Q0=makeQuery(id+"F5.imprint","IMPRINT",FACE,{"disambiguationData":[TD([[makeQuery(id+"F5.imprint","IMPRINT",EDGE,{"derivedFrom":sQuery(id+"F5.wireOp",EDGE,"E13.0.0")}),-1.0]])]});
            extrude(context, id + "F6", {"entities" : qUnion([Q0]), "depth" : 25.4 * mm});
        }
        {
            var Q0;
            Q0=makeQuery(id+"F1.opExtrude","CAP_FACE",FACE,{"disambiguationData":[OSD([sQuery(id+"F0.wireOp",EDGE,"E0"),sQuery(id+"F0.wireOp",EDGE,"E1"),sQuery(id+"F0.wireOp",EDGE,"E2.left"),sQuery(id+"F0.wireOp",EDGE,"E2.right"),sQuery(id+"F0.wireOp",EDGE,"E3.bottom"),sQuery(id+"F0.wireOp",EDGE,"E3.top"),sQuery(id+"F0.wireOp",EDGE,"E3.right"),sQuery(id+"F0.wireOp",EDGE,"E4.trimOffspring"),sQuery(id+"F0.wireOp",EDGE,"E5.1.1"),sQuery(id+"F0.wireOp",EDGE,"E5.1.2"),sQuery(id+"F0.wireOp",EDGE,"E5.1.3"),sQuery(id+"F0.wireOp",EDGE,"E5.1.4"),sQuery(id+"F0.wireOp",EDGE,"E5.1.5"),sQuery(id+"F0.wireOp",EDGE,"E5.1.6"),sQuery(id+"F0.wireOp",EDGE,"E5.1.7"),sQuery(id+"F0.wireOp",EDGE,"E5.2.2"),sQuery(id+"F0.wireOp",EDGE,"E5.2.3"),sQuery(id+"F0.wireOp",EDGE,"E5.2.4"),sQuery(id+"F0.wireOp",EDGE,"E5.2.5"),sQuery(id+"F0.wireOp",EDGE,"E5.2.6"),sQuery(id+"F0.wireOp",EDGE,"E5.2.7"),sQuery(id+"F0.wireOp",EDGE,"E5.3.1"),sQuery(id+"F0.wireOp",EDGE,"E5.3.2"),sQuery(id+"F0.wireOp",EDGE,"E5.3.3"),sQuery(id+"F0.wireOp",EDGE,"E5.3.4"),sQuery(id+"F0.wireOp",EDGE,"E5.3.5"),sQuery(id+"F0.wireOp",EDGE,"E5.3.6"),sQuery(id+"F0.wireOp",EDGE,"E5.3.7"),sQuery(id+"F0.wireOp",EDGE,"E5.4.1"),sQuery(id+"F0.wireOp",EDGE,"E5.4.2"),sQuery(id+"F0.wireOp",EDGE,"E5.4.3"),sQuery(id+"F0.wireOp",EDGE,"E5.4.4"),sQuery(id+"F0.wireOp",EDGE,"E5.4.5"),sQuery(id+"F0.wireOp",EDGE,"E5.4.6"),sQuery(id+"F0.wireOp",EDGE,"E5.4.7"),sQuery(id+"F0.wireOp",EDGE,"E6.3.5.0"),sQuery(id+"F0.wireOp",EDGE,"E6.6.5.0"),sQuery(id+"F0.wireOp",EDGE,"E6.10.5.0"),sQuery(id+"F0.wireOp",EDGE,"E6.13.5.0"),sQuery(id+"F0.wireOp",EDGE,"E6.16.5.0"),sQuery(id+"F0.wireOp",EDGE,"E6.19.5.0"),sQuery(id+"F0.wireOp",EDGE,"E6.22.5.0"),sQuery(id+"F0.wireOp",EDGE,"E7"),sQuery(id+"F0.wireOp",EDGE,"E8.trimOffspring"),sQuery(id+"F0.wireOp",EDGE,"E9.trimOffspring"),sQuery(id+"F0.wireOp",EDGE,"E10.trimOffspring"),sQuery(id+"F0.wireOp",EDGE,"E11.trimOffspring"),sQuery(id+"F0.wireOp",EDGE,"E12.trimOffspring")])],"isStart":false});
            var sketch = newSketch(context, id + "F7", { "sketchPlane" : qUnion([Q0])});
            skLineSegment(sketch, "E15.0.0", {"start": v(-24.4, 20.32) * mm, "end": v(-43.52, 31.27) * mm});
            skArc(sketch, "E15.0.1", {"start": v(-43.52, 31.27) * mm, "mid": v(-44.44, 31.4) * mm, "end": v(-45.2, 30.88) * mm});
            skArc(sketch, "E15.0.2", {"start": v(-45.2, 30.88) * mm, "mid": v(-47.47, 27.27) * mm, "end": v(-49.44, 23.5) * mm});
            skArc(sketch, "E15.0.3", {"start": v(-49.44, 23.5) * mm, "mid": v(-49.5, 22.57) * mm, "end": v(-48.93, 21.85) * mm});
            skLineSegment(sketch, "E15.0.4", {"start": v(-48.93, 21.85) * mm, "end": v(-42.04, 17.9) * mm});
            skLineSegment(sketch, "E15.0.5", {"start": v(-42.04, 17.9) * mm, "end": v(-48.29, 7.08) * mm});
            skArc(sketch, "E15.0.6", {"start": v(-48.29, 7.08) * mm, "mid": v(-48.42, 6.12) * mm, "end": v(-47.82, 5.34) * mm});
            skLineSegment(sketch, "E15.0.7", {"start": v(-47.82, 5.34) * mm, "end": v(-43.74, 2.98) * mm});
            skArc(sketch, "E15.0.8", {"start": v(-43.74, 2.98) * mm, "mid": v(-42.77, 2.86) * mm, "end": v(-42, 3.45) * mm});
            skLineSegment(sketch, "E15.0.9", {"start": v(-42, 3.45) * mm, "end": v(-35.74, 14.3) * mm});
            skLineSegment(sketch, "E15.0.10", {"start": v(-35.74, 14.3) * mm, "end": v(-29.81, 10.92) * mm});
            skArc(sketch, "E15.0.11", {"start": v(-29.81, 10.92) * mm, "mid": v(-31.74, -0.62) * mm, "end": v(-29.37, -12.07) * mm});
            skLineSegment(sketch, "E15.0.12", {"start": v(-29.37, -12.07) * mm, "end": v(-48.76, -22.08) * mm});
            skArc(sketch, "E15.0.13", {"start": v(-48.76, -22.08) * mm, "mid": v(-49.38, -22.8) * mm, "end": v(-49.32, -23.76) * mm});
            skArc(sketch, "E15.0.14", {"start": v(-49.32, -23.76) * mm, "mid": v(-47.34, -27.5) * mm, "end": v(-45.07, -31.07) * mm});
            skArc(sketch, "E15.0.15", {"start": v(-45.07, -31.07) * mm, "mid": v(-44.3, -31.59) * mm, "end": v(-43.39, -31.45) * mm});
            skLineSegment(sketch, "E15.0.16", {"start": v(-43.39, -31.45) * mm, "end": v(-36.53, -27.45) * mm});
            skLineSegment(sketch, "E15.0.17", {"start": v(-36.53, -27.45) * mm, "end": v(-30.28, -38.28) * mm});
            skArc(sketch, "E15.0.18", {"start": v(-30.28, -38.28) * mm, "mid": v(-29.5, -38.87) * mm, "end": v(-28.54, -38.75) * mm});
            skLineSegment(sketch, "E15.0.19", {"start": v(-28.54, -38.75) * mm, "end": v(-24.45, -36.39) * mm});
            skArc(sketch, "E15.0.20", {"start": v(-24.45, -36.39) * mm, "mid": v(-23.86, -35.61) * mm, "end": v(-23.99, -34.65) * mm});
            skLineSegment(sketch, "E15.0.21", {"start": v(-23.99, -34.65) * mm, "end": v(-30.26, -23.8) * mm});
            skLineSegment(sketch, "E15.0.22", {"start": v(-30.26, -23.8) * mm, "end": v(-24.36, -20.36) * mm});
            skArc(sketch, "E15.0.23", {"start": v(-24.36, -20.36) * mm, "mid": v(-15.85, -27.5) * mm, "end": v(-5.4, -31.29) * mm});
            skLineSegment(sketch, "E15.0.24", {"start": v(-5.4, -31.29) * mm, "end": v(-5.32, -53.32) * mm});
            skArc(sketch, "E15.0.25", {"start": v(-5.32, -53.32) * mm, "mid": v(-4.98, -54.19) * mm, "end": v(-4.14, -54.59) * mm});
            skArc(sketch, "E15.0.26", {"start": v(-4.14, -54.59) * mm, "mid": v(0.12, -54.74) * mm, "end": v(4.37, -54.57) * mm});
            skArc(sketch, "E15.0.27", {"start": v(4.37, -54.57) * mm, "mid": v(5.2, -54.16) * mm, "end": v(5.54, -53.3) * mm});
            skLineSegment(sketch, "E15.0.28", {"start": v(5.54, -53.3) * mm, "end": v(5.5, -45.36) * mm});
            skLineSegment(sketch, "E15.0.29", {"start": v(5.5, -45.36) * mm, "end": v(18.01, -45.36) * mm});
            skArc(sketch, "E15.0.30", {"start": v(18.01, -45.36) * mm, "mid": v(18.91, -44.99) * mm, "end": v(19.28, -44.1) * mm});
            skLineSegment(sketch, "E15.0.31", {"start": v(19.28, -44.1) * mm, "end": v(19.28, -39.37) * mm});
            skArc(sketch, "E15.0.32", {"start": v(19.28, -39.37) * mm, "mid": v(18.91, -38.47) * mm, "end": v(18.01, -38.1) * mm});
            skLineSegment(sketch, "E15.0.33", {"start": v(18.01, -38.1) * mm, "end": v(5.48, -38.1) * mm});
            skLineSegment(sketch, "E15.0.34", {"start": v(5.48, -38.1) * mm, "end": v(5.45, -31.28) * mm});
            skArc(sketch, "E15.0.35", {"start": v(5.45, -31.28) * mm, "mid": v(15.9, -27.48) * mm, "end": v(24.4, -20.32) * mm});
            skLineSegment(sketch, "E15.0.36", {"start": v(24.4, -20.32) * mm, "end": v(44.53, -31.84) * mm});
            skArc(sketch, "E15.0.37", {"start": v(44.53, -31.84) * mm, "mid": v(47.17, -27.78) * mm, "end": v(49.44, -23.5) * mm});
            skArc(sketch, "E15.0.38", {"start": v(49.44, -23.5) * mm, "mid": v(49.5, -22.57) * mm, "end": v(48.93, -21.85) * mm});
            skLineSegment(sketch, "E15.0.39", {"start": v(48.93, -21.85) * mm, "end": v(42.04, -17.9) * mm});
            skLineSegment(sketch, "E15.0.40", {"start": v(42.04, -17.9) * mm, "end": v(48.29, -7.08) * mm});
            skArc(sketch, "E15.0.41", {"start": v(48.29, -7.08) * mm, "mid": v(48.42, -6.12) * mm, "end": v(47.82, -5.34) * mm});
            skLineSegment(sketch, "E15.0.42", {"start": v(47.82, -5.34) * mm, "end": v(43.74, -2.98) * mm});
            skArc(sketch, "E15.0.43", {"start": v(43.74, -2.98) * mm, "mid": v(42.77, -2.86) * mm, "end": v(42, -3.45) * mm});
            skLineSegment(sketch, "E15.0.44", {"start": v(42, -3.45) * mm, "end": v(35.74, -14.3) * mm});
            skLineSegment(sketch, "E15.0.45", {"start": v(35.74, -14.3) * mm, "end": v(29.81, -10.92) * mm});
            skArc(sketch, "E15.0.46", {"start": v(29.81, -10.92) * mm, "mid": v(31.75, 0.03) * mm, "end": v(29.8, 10.96) * mm});
            skLineSegment(sketch, "E15.0.47", {"start": v(29.8, 10.96) * mm, "end": v(48.84, 22.06) * mm});
            skArc(sketch, "E15.0.48", {"start": v(48.84, 22.06) * mm, "mid": v(49.41, 22.78) * mm, "end": v(49.34, 23.7) * mm});
            skArc(sketch, "E15.0.49", {"start": v(49.34, 23.7) * mm, "mid": v(47.35, 27.47) * mm, "end": v(45.07, 31.07) * mm});
            skArc(sketch, "E15.0.50", {"start": v(45.07, 31.07) * mm, "mid": v(44.3, 31.59) * mm, "end": v(43.39, 31.45) * mm});
            skLineSegment(sketch, "E15.0.51", {"start": v(43.39, 31.45) * mm, "end": v(36.53, 27.45) * mm});
            skLineSegment(sketch, "E15.0.52", {"start": v(36.53, 27.45) * mm, "end": v(30.28, 38.28) * mm});
            skArc(sketch, "E15.0.53", {"start": v(30.28, 38.28) * mm, "mid": v(29.5, 38.87) * mm, "end": v(28.54, 38.75) * mm});
            skLineSegment(sketch, "E15.0.54", {"start": v(28.54, 38.75) * mm, "end": v(24.45, 36.39) * mm});
            skArc(sketch, "E15.0.55", {"start": v(24.45, 36.39) * mm, "mid": v(23.86, 35.61) * mm, "end": v(23.99, 34.65) * mm});
            skLineSegment(sketch, "E15.0.56", {"start": v(23.99, 34.65) * mm, "end": v(30.26, 23.8) * mm});
            skLineSegment(sketch, "E15.0.57", {"start": v(30.26, 23.8) * mm, "end": v(24.36, 20.36) * mm});
            skArc(sketch, "E15.0.58", {"start": v(24.36, 20.36) * mm, "mid": v(15.85, 27.5) * mm, "end": v(5.4, 31.29) * mm});
            skLineSegment(sketch, "E15.0.59", {"start": v(5.4, 31.29) * mm, "end": v(5.32, 53.32) * mm});
            skArc(sketch, "E15.0.60", {"start": v(5.32, 53.32) * mm, "mid": v(4.98, 54.19) * mm, "end": v(4.14, 54.59) * mm});
            skArc(sketch, "E15.0.61", {"start": v(4.14, 54.59) * mm, "mid": v(-0.12, 54.74) * mm, "end": v(-4.37, 54.57) * mm});
            skArc(sketch, "E15.0.62", {"start": v(-4.37, 54.57) * mm, "mid": v(-5.2, 54.16) * mm, "end": v(-5.54, 53.3) * mm});
            skLineSegment(sketch, "E15.0.63", {"start": v(-5.54, 53.3) * mm, "end": v(-5.5, 45.36) * mm});
            skLineSegment(sketch, "E15.0.64", {"start": v(-5.5, 45.36) * mm, "end": v(-18.01, 45.36) * mm});
            skArc(sketch, "E15.0.65", {"start": v(-18.01, 45.36) * mm, "mid": v(-18.91, 44.99) * mm, "end": v(-19.28, 44.1) * mm});
            skLineSegment(sketch, "E15.0.66", {"start": v(-19.28, 44.1) * mm, "end": v(-19.28, 39.37) * mm});
            skArc(sketch, "E15.0.67", {"start": v(-19.28, 39.37) * mm, "mid": v(-18.91, 38.47) * mm, "end": v(-18.01, 38.1) * mm});
            skLineSegment(sketch, "E15.0.68", {"start": v(-18.01, 38.1) * mm, "end": v(-5.48, 38.1) * mm});
            skLineSegment(sketch, "E15.0.69", {"start": v(-5.48, 38.1) * mm, "end": v(-5.45, 31.28) * mm});
            skArc(sketch, "E15.0.70", {"start": v(-5.45, 31.28) * mm, "mid": v(-15.9, 27.48) * mm, "end": v(-24.4, 20.32) * mm});
            skSolve(sketch);
        }
        {
            var Q0;
            Q0=makeQuery(id+"F7.imprint","IMPRINT",FACE,{"disambiguationData":[TD([[makeQuery(id+"F7.imprint","IMPRINT",EDGE,{"derivedFrom":sQuery(id+"F7.wireOp",EDGE,"E15.0.0")}),1.0]])]});
            extrude(context, id + "F8", {"entities" : qUnion([Q0]), "operationType" : NewBodyOperationType.REMOVE, "oppositeDirection" : true, "depth" : 25.4 * mm});
        }
        {
            var Q0;
            Q0=makeQuery(id+"F6.opExtrude","SWEPT_EDGE",EDGE,{"disambiguationData":[OSD([sQuery(id+"F5.wireOp",EDGE,"E14.42"),sQuery(id+"F5.wireOp",EDGE,"E14.43")])]});
            fillet(context, id + "F9", {"entities" : qUnion([Q0]), "radius" : 5.08 * mm, "tangentPropagation" : true, "allowEdgeOverflow" : false});
        }
        {
            var Q0;
            Q0=makeQuery(id+"F6.opExtrude","SWEPT_EDGE",EDGE,{"disambiguationData":[OSD([sQuery(id+"F5.wireOp",EDGE,"E13.0.36"),sQuery(id+"F5.wireOp",EDGE,"E13.0.37")])]});
            fillet(context, id + "F10", {"entities" : qUnion([Q0]), "radius" : 1.78 * mm, "tangentPropagation" : true, "allowEdgeOverflow" : false});
        }
    });
